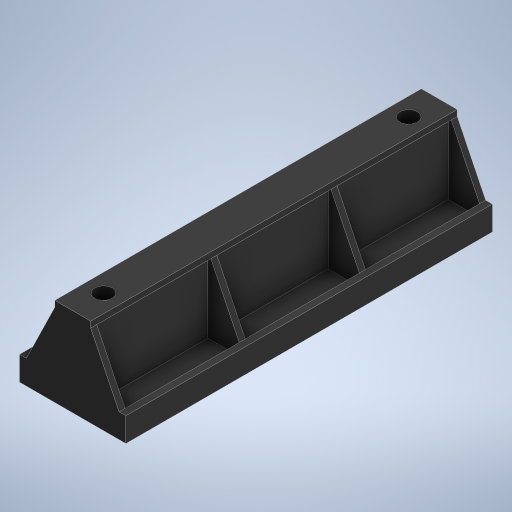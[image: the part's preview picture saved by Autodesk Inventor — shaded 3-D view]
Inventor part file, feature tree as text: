
AUTODESK INVENTOR PART (.ipt)
format: ipt  version: 2024 (Build 280153000, 153)  size: 496,640 bytes
history: native  units: in
note: dims shown in document units (in); Inventor stores cm internally (conversion verified against a paired STEP export)
features: sketch x9, projected_geometry x9, extrude x7, mirror x6, plane x4, loft x1
ambient origin geometry x8: Origin, YZ Plane, XZ Plane, XY Plane, X Axis, Y Axis, Z Axis, Center Point
bodies: Solid1 (feature_tree)
feature tree (36):
  plane  "Work Plane1"
  extrude  "Extrusion2"  Depth=0.4in
  extrude  "Extrusion3"  Depth=0.4in
  mirror  "Mirror1"
  mirror  "Mirror2"
  extrude  "Extrusion4"  Depth=0.0625in
  extrude  "Extrusion5"  Depth=0.0625in
  extrude  "Extrusion6"  Depth=1.184in
  extrude  "Extrusion7"  Depth=1.184in
  extrude  "Extrusion8"  Depth=0.0625in
  plane  "Work Plane2"
  mirror  "Mirror3"
  plane  "Work Plane3"
  loft  "Loft2"
  plane  "Work Plane5"
  mirror  "Mirror7"
  mirror  "Mirror8"
  mirror  "Mirror9"
  sketch  "Sketch2"  dims[d7=0.4in d8=0.4in]
  sketch  "Sketch4"  dims[d9=0.4in d10=0.4in]
  projected_geometry  "Projected Loop1"
  sketch  "Sketch5"  dims[d11=0.125in d12=0.0in d20=0.0625in]
  projected_geometry  "Projected Loop2"
  projected_geometry  "Projected Loop3"
  projected_geometry  "Projected Loop4"
  sketch  "Sketch6"  dims[d21=0.0625in d22=0.592in]
  projected_geometry  "Projected Loop5"
  projected_geometry  "Projected Loop6"
  sketch  "Sketch7"  dims[d23=0.326in d24=1.184in]
  projected_geometry  "Projected Loop7"
  sketch  "Sketch8"  dims[d25=0.0625in d26=1.184in]
  projected_geometry  "Projected Loop8"
  sketch  "Sketch9"  dims[d27=0.326in d28=0.0625in]
  projected_geometry  "Projected Loop9"
  sketch  "Sketch12"  dims[d29=0.0625in d30=0.125in d31=0.0in]
  sketch  "Sketch13"  dims[d32=0.125in d33=0.0in d34=0.125in d35=0.0in d36=0.605in d37=0.0in d38=0.0312in d39=0.0312in d40=0.0625in d41=0.0in d43=0.0312in d44=0.0in d45=-0.155in d50=0.592in d56=0.0in d57=90.0deg d58=0.0in d59=90.0deg d60=0.592in]
